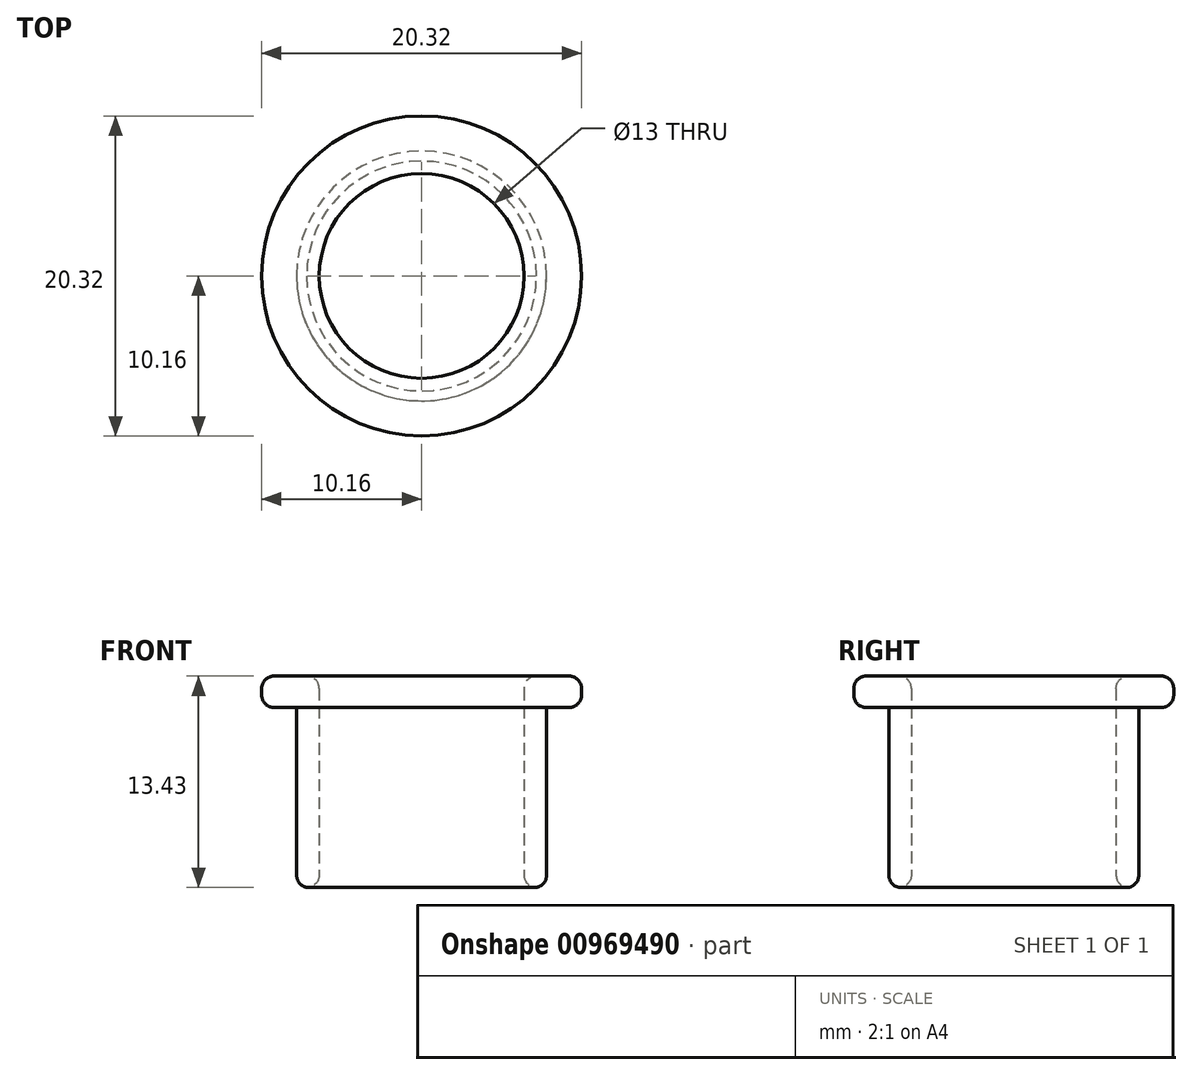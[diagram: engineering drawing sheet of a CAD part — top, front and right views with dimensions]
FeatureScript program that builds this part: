
annotation { "Feature Type Name" : "Feature", "Feature Type Description" : "" }
export const myFeature = defineFeature(function(context is Context, id is Id, definition is map)
    precondition{}
    {
        {
            var Q0;
            Q0=qCreatedBy(makeId("Top.planeOp"),FACE);
            var sketch = newSketch(context, id + "F0", { "sketchPlane" : qUnion([Q0])});
            skCircle(sketch, "E0", {"center": v(0, 0) * mm, "radius": 6.5 * mm});
            skCircle(sketch, "E1", {"center": v(0, 0) * mm, "radius": 7.94 * mm});
            skSolve(sketch);
        }
        {
            var Q0;
            Q0 = qSketchRegion(id + "F0", true);
            extrude(context, id + "F1", {"entities" : qUnion([Q0]), "depth" : 11.43 * mm, "offsetDistance" : 25 * mm});
        }
        {
            var Q0;
            Q0=makeQuery(id+"F1.opExtrude","CAP_FACE",FACE,{"disambiguationData":[OSD([sQuery(id+"F0.wireOp",EDGE,"E0"),sQuery(id+"F0.wireOp",EDGE,"E1")])],"isStart":false});
            var sketch = newSketch(context, id + "F2", { "sketchPlane" : qUnion([Q0])});
            skCircle(sketch, "E2", {"center": v(0, 0) * mm, "radius": 10.16 * mm});
            skCircle(sketch, "E3", {"center": v(0, 0) * mm, "radius": 6.5 * mm});
            skSolve(sketch);
        }
        {
            var Q0;
            Q0 = qSketchRegion(id + "F2", true);
            extrude(context, id + "F3", {"entities" : qUnion([Q0]), "operationType" : NewBodyOperationType.ADD, "depth" : 2 * mm, "offsetDistance" : 25 * mm});
        }
        {
            var Q0;
            Q0=makeQuery(id+"F3.opExtrude","CAP_EDGE",EDGE,{"disambiguationData":[OSD([sQuery(id+"F2.wireOp",EDGE,"E3")])],"isStart":false});
            var Q1;
            Q1=makeQuery(id+"F1.opExtrude","CAP_EDGE",EDGE,{"disambiguationData":[OSD([sQuery(id+"F0.wireOp",EDGE,"E0")])],"isStart":true});
            var Q2;
            Q2=makeQuery(id+"F1.opExtrude","CAP_EDGE",EDGE,{"disambiguationData":[OSD([sQuery(id+"F0.wireOp",EDGE,"E1")])],"isStart":false});
            var Q3;
            Q3=makeQuery(id+"F3.opExtrude","CAP_EDGE",EDGE,{"disambiguationData":[OSD([sQuery(id+"F2.wireOp",EDGE,"E2")])],"isStart":false});
            fillet(context, id + "F4", {"entities" : qUnion([Q0, Q1, Q2, Q3]), "radius" : .8 * mm, "tangentPropagation" : true, "allowEdgeOverflow" : false});
        }
        {
            var Q0;
            Q0=makeQuery(id+"F1.opExtrude","CAP_EDGE",EDGE,{"disambiguationData":[OSD([sQuery(id+"F0.wireOp",EDGE,"E1")])],"isStart":true});
            var Q1;
            Q1=makeQuery(id+"F3.opExtrude","CAP_EDGE",EDGE,{"disambiguationData":[OSD([sQuery(id+"F2.wireOp",EDGE,"E2")])],"isStart":true});
            fillet(context, id + "F5", {"entities" : qUnion([Q0, Q1]), "radius" : .8 * mm, "tangentPropagation" : true, "allowEdgeOverflow" : false});
        }
    });
